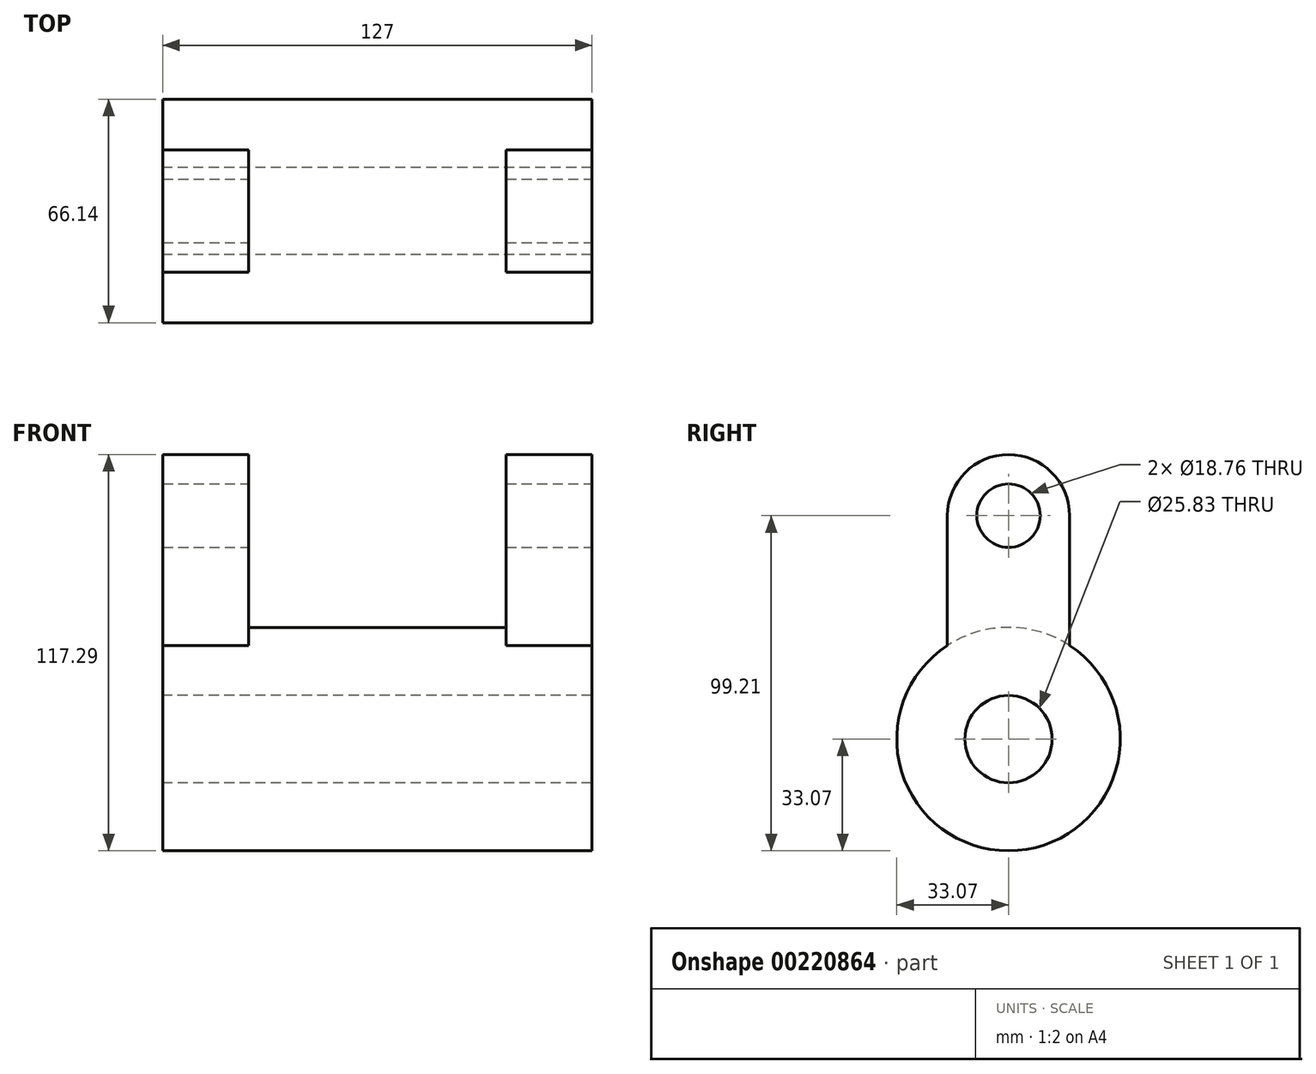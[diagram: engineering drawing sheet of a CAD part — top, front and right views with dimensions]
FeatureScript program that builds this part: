
annotation { "Feature Type Name" : "Feature", "Feature Type Description" : "" }
export const myFeature = defineFeature(function(context is Context, id is Id, definition is map)
    precondition{}
    {
        {
            var Q0;
            Q0=qCreatedBy(makeId("Right.planeOp"),FACE);
            var sketch = newSketch(context, id + "F0", { "sketchPlane" : qUnion([Q0])});
            skCircle(sketch, "E0", {"center": v(0, 0) * mm, "radius": 33.07 * mm});
            skSolve(sketch);
        }
        {
            var Q0;
            Q0=makeQuery(id+"F0.imprint","IMPRINT",FACE,{"disambiguationData":[TD([[makeQuery(id+"F0.imprint","IMPRINT",EDGE,{"derivedFrom":sQuery(id+"F0.wireOp",EDGE,"E0")}),1.0]])]});
            extrude(context, id + "F1", {"entities" : qUnion([Q0]), "oppositeDirection" : true, "depth" : 63.5 * mm});
        }
        {
            var Q0;
            Q0=makeQuery(id+"F1.opExtrude","CAP_FACE",FACE,{"disambiguationData":[OSD([sQuery(id+"F0.wireOp",EDGE,"E0")])],"isStart":true});
            var sketch = newSketch(context, id + "F2", { "sketchPlane" : qUnion([Q0])});
            skLineSegment(sketch, "E1.bottom", {"start": v(-18.08, 0) * mm, "end": v(18.08, 0) * mm});
            skLineSegment(sketch, "E1.top", {"start": v(-18.08, 66.14) * mm, "end": v(18.08, 66.14) * mm});
            skLineSegment(sketch, "E1.left", {"start": v(-18.08, 0) * mm, "end": v(-18.08, 66.14) * mm});
            skLineSegment(sketch, "E1.right", {"start": v(18.08, 0) * mm, "end": v(18.08, 66.14) * mm});
            skPoint(sketch, "E1.middle", {"position": v(0, 33.07) * mm});
            skSolve(sketch);
        }
        {
            var Q0;
            {var subQ0=sQuery(id+"F2.wireOp",EDGE,"E1.top");Q0=makeQuery(id+"F2.imprint","IMPRINT",FACE,{"disambiguationData":[TD([[makeQuery(id+"F2.imprint","IMPRINT",EDGE,{"derivedFrom":subQ0}),-1.0]])]});}
            var Q1;
            {var subQ0=sQuery(id+"F2.wireOp",EDGE,"E1.bottom");Q1=makeQuery(id+"F2.imprint","IMPRINT",FACE,{"disambiguationData":[TD([[makeQuery(id+"F2.imprint","IMPRINT",EDGE,{"derivedFrom":subQ0}),1.0]])]});}
            extrude(context, id + "F3", {"entities" : qUnion([Q0, Q1]), "operationType" : NewBodyOperationType.ADD, "oppositeDirection" : true, "depth" : 25.4 * mm});
        }
        {
            var Q0;
            Q0=makeQuery(id+"F1.opExtrude","SWEPT_BODY",BODY,{"disambiguationData":[OSD([sQuery(id+"F0.wireOp",EDGE,"E0")])]});
            var Q1;
            Q1=makeQuery(id+"F1.opExtrude","CAP_FACE",FACE,{"disambiguationData":[OSD([sQuery(id+"F0.wireOp",EDGE,"E0")])],"isStart":false});
            mirror(context, id + "F4", {"operationType" : NewBodyOperationType.ADD, "entities" : qUnion([Q0]), "mirrorPlane" : qUnion([Q1])});
        }
        {
            var Q0;
            Q0=makeQuery(id+"F3.boolean.opBoolean","MERGE",FACE,{"derivedFrom":[makeQuery(id+"F1.opExtrude","CAP_FACE",FACE,{"disambiguationData":[OSD([sQuery(id+"F0.wireOp",EDGE,"E0")])],"isStart":true}),makeQuery(id+"F3.opExtrude","CAP_FACE",FACE,{"disambiguationData":[OSD([sQuery(id+"F2.wireOp",EDGE,"E1.bottom"),sQuery(id+"F2.wireOp",EDGE,"E1.top"),sQuery(id+"F2.wireOp",EDGE,"E1.left"),sQuery(id+"F2.wireOp",EDGE,"E1.right")])],"isStart":true})]});
            var sketch = newSketch(context, id + "F5", { "sketchPlane" : qUnion([Q0])});
            skCircle(sketch, "E2", {"center": v(0, 66.14) * mm, "radius": 18.08 * mm});
            skSolve(sketch);
        }
        {
            var Q0;
            Q0=makeQuery(id+"F4.opPattern","COPY",FACE,{"derivedFrom":makeQuery(id+"F3.boolean.opBoolean","MERGE",FACE,{"derivedFrom":[makeQuery(id+"F1.opExtrude","CAP_FACE",FACE,{"disambiguationData":[OSD([sQuery(id+"F0.wireOp",EDGE,"E0")])],"isStart":true}),makeQuery(id+"F3.opExtrude","CAP_FACE",FACE,{"disambiguationData":[OSD([sQuery(id+"F2.wireOp",EDGE,"E1.bottom"),sQuery(id+"F2.wireOp",EDGE,"E1.top"),sQuery(id+"F2.wireOp",EDGE,"E1.left"),sQuery(id+"F2.wireOp",EDGE,"E1.right")])],"isStart":true})]}),"instanceName":"1"});
            var sketch = newSketch(context, id + "F6", { "sketchPlane" : qUnion([Q0])});
            skCircle(sketch, "E3", {"center": v(0, 66.14) * mm, "radius": 18.08 * mm});
            skSolve(sketch);
        }
        {
            var Q0;
            {var subQ1=makeQuery(id+"F3.opExtrude","CAP_EDGE",EDGE,{"disambiguationData":[OSD([sQuery(id+"F2.wireOp",EDGE,"E1.top")])],"isStart":true});Q0=makeQuery(id+"F5.imprint","IMPRINT",FACE,{"disambiguationData":[TD([[makeQuery(id+"F5.imprint","IMPRINT",EDGE,{"derivedFrom":subQ1}),-1.0]])]});}
            var Q1;
            {var subQ1=makeQuery(id+"F3.opExtrude","CAP_EDGE",EDGE,{"disambiguationData":[OSD([sQuery(id+"F2.wireOp",EDGE,"E1.top")])],"isStart":true});Q1=makeQuery(id+"F5.imprint","IMPRINT",FACE,{"disambiguationData":[TD([[makeQuery(id+"F5.imprint","IMPRINT",EDGE,{"derivedFrom":subQ1}),1.0]])]});}
            extrude(context, id + "F7", {"entities" : qUnion([Q0, Q1]), "operationType" : NewBodyOperationType.ADD, "oppositeDirection" : true, "depth" : 25.4 * mm});
        }
        {
            var Q0;
            {var subQ1=makeQuery(id+"F4.opPattern","COPY",EDGE,{"derivedFrom":makeQuery(id+"F3.opExtrude","CAP_EDGE",EDGE,{"disambiguationData":[OSD([sQuery(id+"F2.wireOp",EDGE,"E1.top")])],"isStart":true}),"instanceName":"1"});Q0=makeQuery(id+"F6.imprint","IMPRINT",FACE,{"disambiguationData":[TD([[makeQuery(id+"F6.imprint","IMPRINT",EDGE,{"derivedFrom":subQ1}),1.0]])]});}
            var Q1;
            {var subQ1=makeQuery(id+"F4.opPattern","COPY",EDGE,{"derivedFrom":makeQuery(id+"F3.opExtrude","CAP_EDGE",EDGE,{"disambiguationData":[OSD([sQuery(id+"F2.wireOp",EDGE,"E1.top")])],"isStart":true}),"instanceName":"1"});Q1=makeQuery(id+"F6.imprint","IMPRINT",FACE,{"disambiguationData":[TD([[makeQuery(id+"F6.imprint","IMPRINT",EDGE,{"derivedFrom":subQ1}),-1.0]])]});}
            extrude(context, id + "F8", {"entities" : qUnion([Q0, Q1]), "operationType" : NewBodyOperationType.ADD, "oppositeDirection" : true, "depth" : 25.4 * mm});
        }
        {
            var Q0;
            Q0=makeQuery(id+"F8.boolean.opBoolean","MERGE",FACE,{"derivedFrom":[makeQuery(id+"F4.opPattern","COPY",FACE,{"derivedFrom":makeQuery(id+"F3.boolean.opBoolean","MERGE",FACE,{"derivedFrom":[makeQuery(id+"F1.opExtrude","CAP_FACE",FACE,{"disambiguationData":[OSD([sQuery(id+"F0.wireOp",EDGE,"E0")])],"isStart":true}),makeQuery(id+"F3.opExtrude","CAP_FACE",FACE,{"disambiguationData":[OSD([sQuery(id+"F2.wireOp",EDGE,"E1.bottom"),sQuery(id+"F2.wireOp",EDGE,"E1.top"),sQuery(id+"F2.wireOp",EDGE,"E1.left"),sQuery(id+"F2.wireOp",EDGE,"E1.right")])],"isStart":true})]}),"instanceName":"1"}),makeQuery(id+"F8.opExtrude","CAP_FACE",FACE,{"disambiguationData":[OSD([sQuery(id+"F6.wireOp",EDGE,"E3")])],"isStart":true})]});
            var sketch = newSketch(context, id + "F9", { "sketchPlane" : qUnion([Q0])});
            skCircle(sketch, "E4", {"center": v(0, 0) * mm, "radius": 12.92 * mm});
            skSolve(sketch);
        }
        {
            var Q0;
            Q0=makeQuery(id+"F9.imprint","IMPRINT",FACE,{"disambiguationData":[TD([[makeQuery(id+"F9.imprint","IMPRINT",EDGE,{"derivedFrom":sQuery(id+"F9.wireOp",EDGE,"E4")}),1.0]])]});
            extrude(context, id + "F10", {"entities" : qUnion([Q0]), "operationType" : NewBodyOperationType.REMOVE, "endBound" : BoundingType.THROUGH_ALL, "oppositeDirection" : true, "depth" : 127 * mm});
        }
        {
            var Q0;
            Q0=makeQuery(id+"F7.boolean.opBoolean","MERGE",FACE,{"derivedFrom":[makeQuery(id+"F3.boolean.opBoolean","MERGE",FACE,{"derivedFrom":[makeQuery(id+"F1.opExtrude","CAP_FACE",FACE,{"disambiguationData":[OSD([sQuery(id+"F0.wireOp",EDGE,"E0")])],"isStart":true}),makeQuery(id+"F3.opExtrude","CAP_FACE",FACE,{"disambiguationData":[OSD([sQuery(id+"F2.wireOp",EDGE,"E1.bottom"),sQuery(id+"F2.wireOp",EDGE,"E1.top"),sQuery(id+"F2.wireOp",EDGE,"E1.left"),sQuery(id+"F2.wireOp",EDGE,"E1.right")])],"isStart":true})]}),makeQuery(id+"F7.opExtrude","CAP_FACE",FACE,{"disambiguationData":[OSD([sQuery(id+"F5.wireOp",EDGE,"E2")])],"isStart":true})]});
            var sketch = newSketch(context, id + "F11", { "sketchPlane" : qUnion([Q0])});
            skCircle(sketch, "E5", {"center": v(0, 66.14) * mm, "radius": 9.38 * mm});
            skSolve(sketch);
        }
        {
            var Q0;
            Q0=makeQuery(id+"F11.imprint","IMPRINT",FACE,{"disambiguationData":[TD([[makeQuery(id+"F11.imprint","IMPRINT",EDGE,{"derivedFrom":sQuery(id+"F11.wireOp",EDGE,"E5")}),1.0]])]});
            extrude(context, id + "F12", {"entities" : qUnion([Q0]), "operationType" : NewBodyOperationType.REMOVE, "endBound" : BoundingType.THROUGH_ALL, "oppositeDirection" : true, "depth" : 127 * mm});
        }
    });
